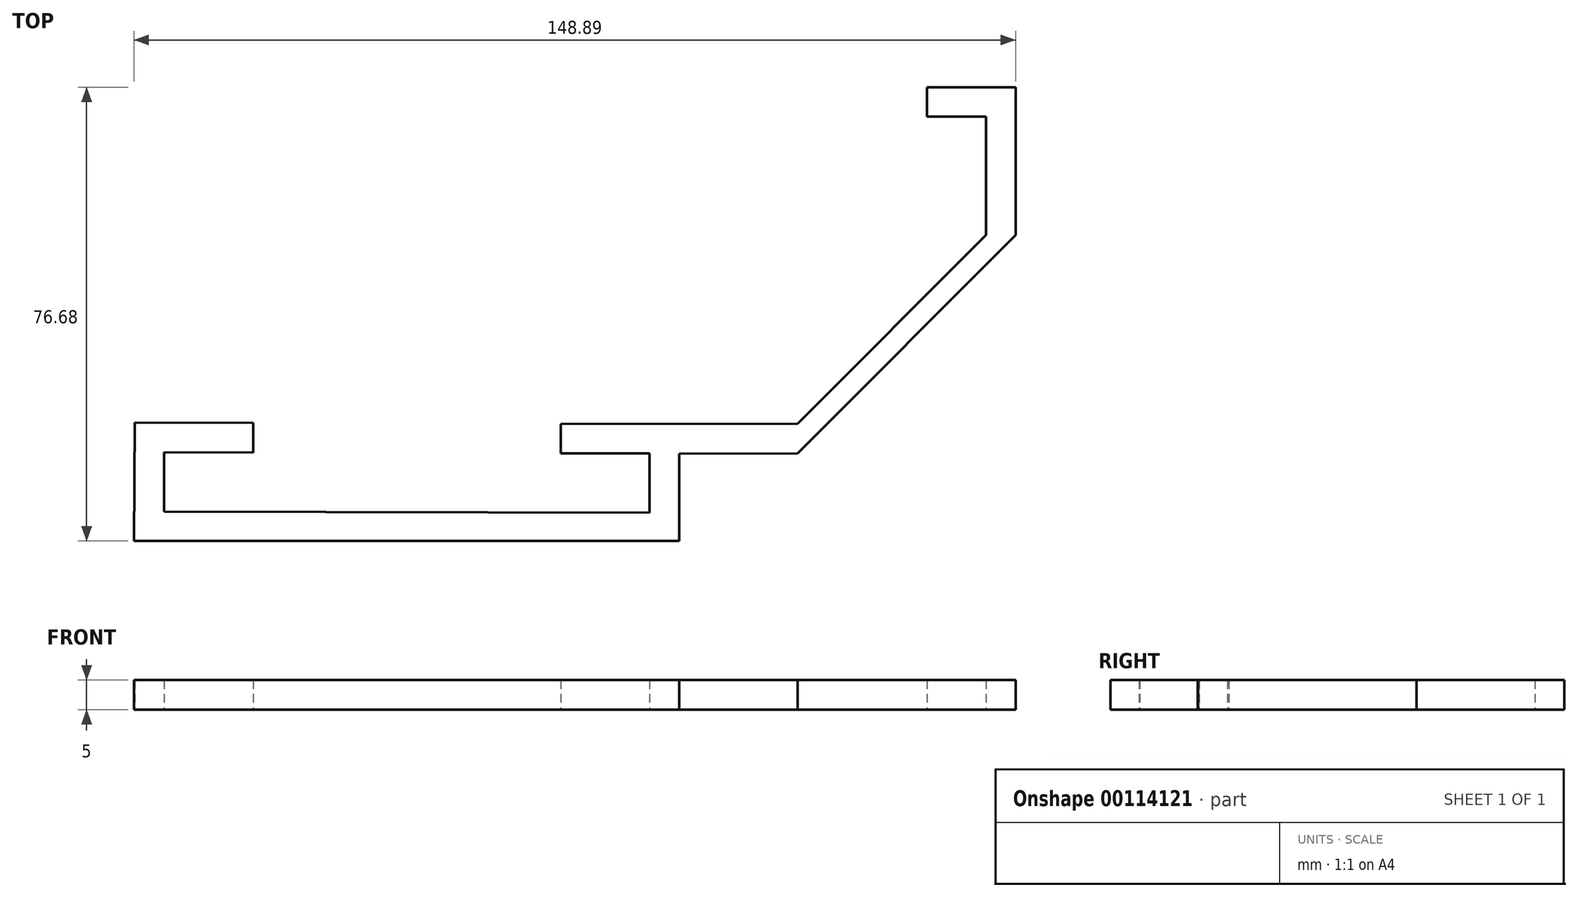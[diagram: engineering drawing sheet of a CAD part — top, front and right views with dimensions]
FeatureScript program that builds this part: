
annotation { "Feature Type Name" : "Feature", "Feature Type Description" : "" }
export const myFeature = defineFeature(function(context is Context, id is Id, definition is map)
    precondition{}
    {
        {
            var Q0;
            Q0=qCreatedBy(makeId("Top.planeOp"),FACE);
            var sketch = newSketch(context, id + "F0", { "sketchPlane" : qUnion([Q0])});
            skLineSegment(sketch, "E0", {"start": v(53.46, 32.8) * mm, "end": v(53.46, 12.8) * mm});
            skLineSegment(sketch, "E1", {"start": v(53.46, 12.8) * mm, "end": v(21.64, -19.03) * mm});
            skLineSegment(sketch, "E2", {"start": v(58.46, 37.8) * mm, "end": v(58.46, 12.8) * mm});
            skLineSegment(sketch, "E3.MirrorCS", {"start": v(-90.43, -38.9) * mm, "end": v(1.65, -38.9) * mm});
            skLineSegment(sketch, "E4.MirrorCS", {"start": v(-85.35, -33.9) * mm, "end": v(-3.35, -34.08) * mm});
            skLineSegment(sketch, "E5.MirrorCS", {"start": v(-85.33, -23.9) * mm, "end": v(-70.33, -23.93) * mm});
            skLineSegment(sketch, "E6", {"start": v(-70.33, -23.93) * mm, "end": v(-70.33, -18.93) * mm});
            skLineSegment(sketch, "E7", {"start": v(-70.33, -18.93) * mm, "end": v(-90.33, -18.9) * mm});
            skLineSegment(sketch, "E8", {"start": v(-85.33, -23.9) * mm, "end": v(-85.35, -33.9) * mm});
            skLineSegment(sketch, "E9", {"start": v(-3.35, -34.08) * mm, "end": v(-3.35, -24.08) * mm});
            skLineSegment(sketch, "E10", {"start": v(-90.33, -18.9) * mm, "end": v(-90.43, -38.9) * mm});
            skLineSegment(sketch, "E11", {"start": v(1.65, -38.9) * mm, "end": v(1.65, -24.15) * mm});
            skLineSegment(sketch, "E12", {"start": v(-3.35, -24.08) * mm, "end": v(-18.35, -24.08) * mm});
            skLineSegment(sketch, "E13", {"start": v(-18.35, -24.08) * mm, "end": v(-18.35, -19.1) * mm});
            skLineSegment(sketch, "E14", {"start": v(-18.35, -19.1) * mm, "end": v(21.64, -19.03) * mm});
            skLineSegment(sketch, "E15", {"start": v(1.65, -24.15) * mm, "end": v(21.65, -24.1) * mm});
            skLineSegment(sketch, "E16", {"start": v(21.65, -24.1) * mm, "end": v(58.46, 12.8) * mm});
            skLineSegment(sketch, "E17", {"start": v(58.46, 37.8) * mm, "end": v(43.46, 37.8) * mm});
            skLineSegment(sketch, "E18", {"start": v(43.46, 37.8) * mm, "end": v(43.46, 32.8) * mm});
            skLineSegment(sketch, "E19", {"start": v(43.46, 32.8) * mm, "end": v(53.46, 32.8) * mm});
            skSolve(sketch);
        }
        {
            var Q0;
            Q0=makeQuery(id+"F0.imprint","IMPRINT",FACE,{"disambiguationData":[TD([[makeQuery(id+"F0.imprint","IMPRINT",EDGE,{"derivedFrom":sQuery(id+"F0.wireOp",EDGE,"E0")}),1.0]])]});
            extrude(context, id + "F1", {"entities" : qUnion([Q0]), "depth" : 5 * mm});
        }
    });
